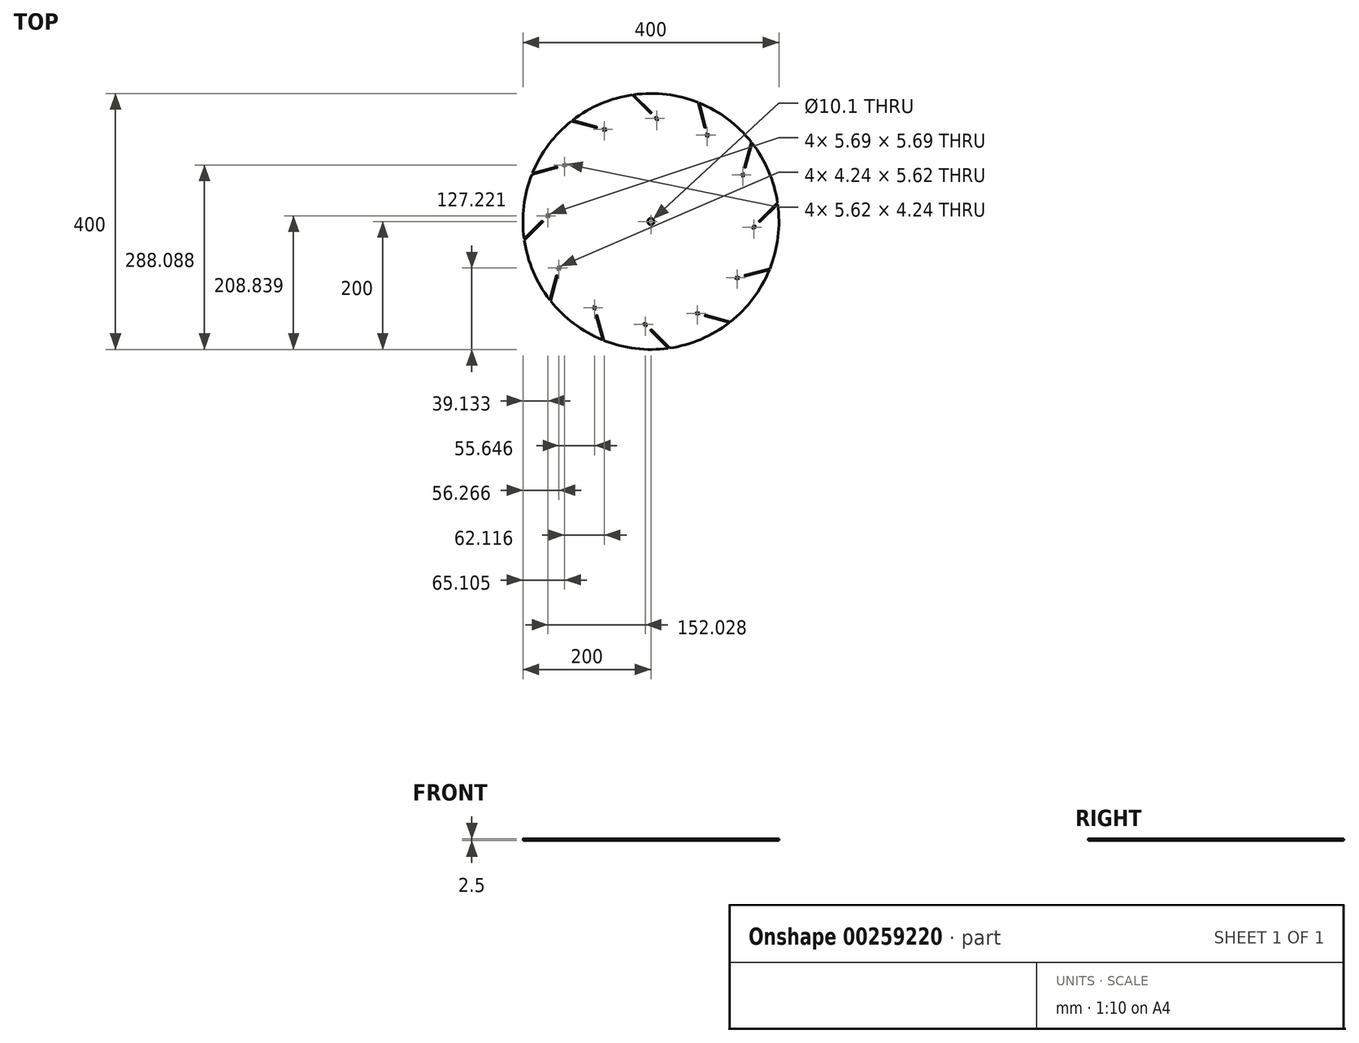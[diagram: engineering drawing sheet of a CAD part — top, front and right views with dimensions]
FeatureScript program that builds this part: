
annotation { "Feature Type Name" : "Feature", "Feature Type Description" : "" }
export const myFeature = defineFeature(function(context is Context, id is Id, definition is map)
    precondition{}
    {
        {
            var Q0;
            Q0=qCreatedBy(makeId("Top.planeOp"),FACE);
            var sketch = newSketch(context, id + "F0", { "sketchPlane" : qUnion([Q0])});
            skArc(sketch, "E0", {"start": v(-197.85, -29.24) * mm, "mid": v(-184.02, -78.33) * mm, "end": v(-158.23, -122.33) * mm});
            skLineSegment(sketch, "E1", {"start": v(28.28, 28.28) * mm, "end": v(-28.28, -28.28) * mm, "construction": true});
            skCircle(sketch, "E2", {"center": v(0, 0) * mm, "radius": 40 * mm, "construction": true});
            skLineSegment(sketch, "E3", {"start": v(40, 0) * mm, "end": v(-286.23, 0) * mm, "construction": true});
            skLineSegment(sketch, "E4", {"start": v(-28.28, -28.28) * mm, "end": v(-235.32, -28.28) * mm, "construction": true});
            skLineSegment(sketch, "E5", {"start": v(-197.99, -28.28) * mm, "end": v(-113.58, 56.13) * mm, "construction": true});
            skPoint(sketch, "E6", {"position": v(-169.7, 0) * mm});
            skCircle(sketch, "E7", {"center": v(0, 0) * mm, "radius": 169.7 * mm, "construction": true});
            skCircle(sketch, "E8", {"center": v(-169.7, 0) * mm, "radius": 0.78 * mm, "construction": true});
            skPoint(sketch, "E9", {"position": v(-197.99, -28.28) * mm});
            skLineSegment(sketch, "E10", {"start": v(-197.44, -28.83) * mm, "end": v(-198.54, -27.74) * mm, "construction": true});
            skCircle(sketch, "E11", {"center": v(-169.7, 0) * mm, "radius": 40 * mm, "construction": true});
            skLineSegment(sketch, "E12.trimOffspring", {"start": v(-170.36, 0.44) * mm, "end": v(-197.62, -26.82) * mm});
            skLineSegment(sketch, "E13.trimOffspring", {"start": v(-169.26, -0.65) * mm, "end": v(-197.85, -29.24) * mm});
            skLineSegment(sketch, "E14", {"start": v(-170.15, 0.44) * mm, "end": v(-169.26, -0.44) * mm});
            skLineSegment(sketch, "E15.MirrorCS", {"start": v(-170.25, 0.55) * mm, "end": v(-141.97, 28.83) * mm, "construction": true});
            skLineSegment(sketch, "E16.MirrorCS", {"start": v(-169.16, -0.55) * mm, "end": v(-140.87, 27.74) * mm, "construction": true});
            skLineSegment(sketch, "E17.MirrorCS", {"start": v(-140.87, 27.74) * mm, "end": v(-141.97, 28.83) * mm, "construction": true});
            skLineSegment(sketch, "E18", {"start": v(-163.71, 8.15) * mm, "end": v(-161.56, 6) * mm});
            skLineSegment(sketch, "E19", {"start": v(-160.18, 11.68) * mm, "end": v(-158.02, 9.53) * mm});
            skLineSegment(sketch, "E20.trimOffspring", {"start": v(-161.56, 6) * mm, "end": v(-158.02, 9.53) * mm});
            skLineSegment(sketch, "E21.trimOffspring", {"start": v(-163.71, 8.15) * mm, "end": v(-160.18, 11.68) * mm});
            skLineSegment(sketch, "E22.trimOffspring", {"start": v(-198.53, -27.73) * mm, "end": v(-198.54, -27.74) * mm});
            skCircle(sketch, "E23", {"center": v(0, 0) * mm, "radius": 5.05 * mm});
            skArc(sketch, "E24", {"start": v(-170.15, 0.44) * mm, "mid": v(-170.25, 0.7) * mm, "end": v(-170.36, 0.44) * mm});
            skArc(sketch, "E25.MirrorC", {"start": v(-169.26, -0.44) * mm, "mid": v(-169, -0.55) * mm, "end": v(-169.26, -0.65) * mm});
            skPoint(sketch, "E26.orphan", {"position": v(-198.12, -27.32) * mm});
            skLineSegment(sketch, "E27.trimOffspring", {"start": v(-197.62, -26.82) * mm, "end": v(-198.2, -26.82) * mm});
            skLineSegment(sketch, "E28.1.0", {"start": v(-184.56, 75.58) * mm, "end": v(-185.05, 75.87) * mm});
            skLineSegment(sketch, "E28.1.1", {"start": v(-147.31, 85.56) * mm, "end": v(-184.56, 75.58) * mm});
            skArc(sketch, "E28.1.2", {"start": v(-147.13, 85.46) * mm, "mid": v(-147.1, 85.73) * mm, "end": v(-147.31, 85.56) * mm});
            skLineSegment(sketch, "E28.1.3", {"start": v(-147.13, 85.46) * mm, "end": v(-146.8, 84.25) * mm});
            skArc(sketch, "E28.1.4", {"start": v(-146.8, 84.25) * mm, "mid": v(-146.64, 84.03) * mm, "end": v(-146.91, 84.07) * mm});
            skLineSegment(sketch, "E28.1.5", {"start": v(-146.91, 84.07) * mm, "end": v(-185.96, 73.6) * mm});
            skLineSegment(sketch, "E28.1.6", {"start": v(-137.7, 88.91) * mm, "end": v(-132.88, 90.2) * mm});
            skLineSegment(sketch, "E28.1.7", {"start": v(-132.88, 90.2) * mm, "end": v(-132.09, 87.26) * mm});
            skLineSegment(sketch, "E28.1.8", {"start": v(-136.92, 85.97) * mm, "end": v(-132.09, 87.26) * mm});
            skLineSegment(sketch, "E28.1.9", {"start": v(-137.7, 88.91) * mm, "end": v(-136.92, 85.97) * mm});
            skLineSegment(sketch, "E28.2.0", {"start": v(-122.04, 157.74) * mm, "end": v(-122.33, 158.23) * mm});
            skLineSegment(sketch, "E28.2.1", {"start": v(-84.8, 147.76) * mm, "end": v(-122.04, 157.74) * mm});
            skArc(sketch, "E28.2.2", {"start": v(-84.7, 147.57) * mm, "mid": v(-84.52, 147.8) * mm, "end": v(-84.8, 147.76) * mm});
            skLineSegment(sketch, "E28.2.3", {"start": v(-84.7, 147.57) * mm, "end": v(-85.01, 146.37) * mm});
            skArc(sketch, "E28.2.4", {"start": v(-85.01, 146.37) * mm, "mid": v(-84.98, 146.1) * mm, "end": v(-85.2, 146.26) * mm});
            skLineSegment(sketch, "E28.2.5", {"start": v(-85.2, 146.26) * mm, "end": v(-124.25, 156.72) * mm});
            skLineSegment(sketch, "E28.2.6", {"start": v(-74.8, 145.85) * mm, "end": v(-69.97, 144.56) * mm});
            skLineSegment(sketch, "E28.2.7", {"start": v(-69.97, 144.56) * mm, "end": v(-70.76, 141.61) * mm});
            skLineSegment(sketch, "E28.2.8", {"start": v(-75.59, 142.9) * mm, "end": v(-70.76, 141.61) * mm});
            skLineSegment(sketch, "E28.2.9", {"start": v(-74.8, 145.85) * mm, "end": v(-75.59, 142.9) * mm});
            skLineSegment(sketch, "E28.3.0", {"start": v(-26.82, 197.62) * mm, "end": v(-26.82, 198.2) * mm});
            skLineSegment(sketch, "E28.3.1", {"start": v(0.44, 170.36) * mm, "end": v(-26.82, 197.62) * mm});
            skArc(sketch, "E28.3.2", {"start": v(0.44, 170.15) * mm, "mid": v(0.7, 170.25) * mm, "end": v(0.44, 170.36) * mm});
            skLineSegment(sketch, "E28.3.3", {"start": v(0.44, 170.15) * mm, "end": v(-0.44, 169.26) * mm});
            skArc(sketch, "E28.3.4", {"start": v(-0.44, 169.26) * mm, "mid": v(-0.55, 169) * mm, "end": v(-0.65, 169.26) * mm});
            skLineSegment(sketch, "E28.3.5", {"start": v(-0.65, 169.26) * mm, "end": v(-29.24, 197.85) * mm});
            skLineSegment(sketch, "E28.3.6", {"start": v(8.15, 163.71) * mm, "end": v(11.68, 160.18) * mm});
            skLineSegment(sketch, "E28.3.7", {"start": v(11.68, 160.18) * mm, "end": v(9.53, 158.02) * mm});
            skLineSegment(sketch, "E28.3.8", {"start": v(6, 161.56) * mm, "end": v(9.53, 158.02) * mm});
            skLineSegment(sketch, "E28.3.9", {"start": v(8.15, 163.71) * mm, "end": v(6, 161.56) * mm});
            skLineSegment(sketch, "E28.4.0", {"start": v(75.58, 184.56) * mm, "end": v(75.87, 185.05) * mm});
            skLineSegment(sketch, "E28.4.1", {"start": v(85.56, 147.31) * mm, "end": v(75.58, 184.56) * mm});
            skArc(sketch, "E28.4.2", {"start": v(85.46, 147.13) * mm, "mid": v(85.73, 147.1) * mm, "end": v(85.56, 147.31) * mm});
            skLineSegment(sketch, "E28.4.3", {"start": v(85.46, 147.13) * mm, "end": v(84.25, 146.8) * mm});
            skArc(sketch, "E28.4.4", {"start": v(84.25, 146.8) * mm, "mid": v(84.03, 146.64) * mm, "end": v(84.07, 146.91) * mm});
            skLineSegment(sketch, "E28.4.5", {"start": v(84.07, 146.91) * mm, "end": v(73.6, 185.96) * mm});
            skLineSegment(sketch, "E28.4.6", {"start": v(88.91, 137.7) * mm, "end": v(90.2, 132.88) * mm});
            skLineSegment(sketch, "E28.4.7", {"start": v(90.2, 132.88) * mm, "end": v(87.26, 132.09) * mm});
            skLineSegment(sketch, "E28.4.8", {"start": v(85.97, 136.92) * mm, "end": v(87.26, 132.09) * mm});
            skLineSegment(sketch, "E28.4.9", {"start": v(88.91, 137.7) * mm, "end": v(85.97, 136.92) * mm});
            skLineSegment(sketch, "E28.5.0", {"start": v(157.74, 122.04) * mm, "end": v(158.23, 122.33) * mm});
            skLineSegment(sketch, "E28.5.1", {"start": v(147.76, 84.8) * mm, "end": v(157.74, 122.04) * mm});
            skArc(sketch, "E28.5.2", {"start": v(147.57, 84.7) * mm, "mid": v(147.8, 84.52) * mm, "end": v(147.76, 84.8) * mm});
            skLineSegment(sketch, "E28.5.3", {"start": v(147.57, 84.7) * mm, "end": v(146.37, 85.01) * mm});
            skArc(sketch, "E28.5.4", {"start": v(146.37, 85.01) * mm, "mid": v(146.1, 84.98) * mm, "end": v(146.26, 85.2) * mm});
            skLineSegment(sketch, "E28.5.5", {"start": v(146.26, 85.2) * mm, "end": v(156.72, 124.25) * mm});
            skLineSegment(sketch, "E28.5.6", {"start": v(145.85, 74.8) * mm, "end": v(144.56, 69.97) * mm});
            skLineSegment(sketch, "E28.5.7", {"start": v(144.56, 69.97) * mm, "end": v(141.61, 70.76) * mm});
            skLineSegment(sketch, "E28.5.8", {"start": v(142.9, 75.59) * mm, "end": v(141.61, 70.76) * mm});
            skLineSegment(sketch, "E28.5.9", {"start": v(145.85, 74.8) * mm, "end": v(142.9, 75.59) * mm});
            skLineSegment(sketch, "E28.6.0", {"start": v(197.62, 26.82) * mm, "end": v(198.2, 26.82) * mm});
            skLineSegment(sketch, "E28.6.1", {"start": v(170.36, -0.44) * mm, "end": v(197.62, 26.82) * mm});
            skArc(sketch, "E28.6.2", {"start": v(170.15, -0.44) * mm, "mid": v(170.25, -0.7) * mm, "end": v(170.36, -0.44) * mm});
            skLineSegment(sketch, "E28.6.3", {"start": v(170.15, -0.44) * mm, "end": v(169.26, 0.44) * mm});
            skArc(sketch, "E28.6.4", {"start": v(169.26, 0.44) * mm, "mid": v(169, 0.55) * mm, "end": v(169.26, 0.65) * mm});
            skLineSegment(sketch, "E28.6.5", {"start": v(169.26, 0.65) * mm, "end": v(197.85, 29.24) * mm});
            skLineSegment(sketch, "E28.6.6", {"start": v(163.71, -8.15) * mm, "end": v(160.18, -11.68) * mm});
            skLineSegment(sketch, "E28.6.7", {"start": v(160.18, -11.68) * mm, "end": v(158.02, -9.53) * mm});
            skLineSegment(sketch, "E28.6.8", {"start": v(161.56, -6) * mm, "end": v(158.02, -9.53) * mm});
            skLineSegment(sketch, "E28.6.9", {"start": v(163.71, -8.15) * mm, "end": v(161.56, -6) * mm});
            skLineSegment(sketch, "E28.7.0", {"start": v(184.56, -75.58) * mm, "end": v(185.05, -75.87) * mm});
            skLineSegment(sketch, "E28.7.1", {"start": v(147.31, -85.56) * mm, "end": v(184.56, -75.58) * mm});
            skArc(sketch, "E28.7.2", {"start": v(147.13, -85.46) * mm, "mid": v(147.1, -85.73) * mm, "end": v(147.31, -85.56) * mm});
            skLineSegment(sketch, "E28.7.3", {"start": v(147.13, -85.46) * mm, "end": v(146.8, -84.25) * mm});
            skArc(sketch, "E28.7.4", {"start": v(146.8, -84.25) * mm, "mid": v(146.64, -84.03) * mm, "end": v(146.91, -84.07) * mm});
            skLineSegment(sketch, "E28.7.5", {"start": v(146.91, -84.07) * mm, "end": v(185.96, -73.6) * mm});
            skLineSegment(sketch, "E28.7.6", {"start": v(137.7, -88.91) * mm, "end": v(132.88, -90.2) * mm});
            skLineSegment(sketch, "E28.7.7", {"start": v(132.88, -90.2) * mm, "end": v(132.09, -87.26) * mm});
            skLineSegment(sketch, "E28.7.8", {"start": v(136.92, -85.97) * mm, "end": v(132.09, -87.26) * mm});
            skLineSegment(sketch, "E28.7.9", {"start": v(137.7, -88.91) * mm, "end": v(136.92, -85.97) * mm});
            skLineSegment(sketch, "E28.8.0", {"start": v(122.04, -157.74) * mm, "end": v(122.33, -158.23) * mm});
            skLineSegment(sketch, "E28.8.1", {"start": v(84.8, -147.76) * mm, "end": v(122.04, -157.74) * mm});
            skArc(sketch, "E28.8.2", {"start": v(84.7, -147.57) * mm, "mid": v(84.52, -147.8) * mm, "end": v(84.8, -147.76) * mm});
            skLineSegment(sketch, "E28.8.3", {"start": v(84.7, -147.57) * mm, "end": v(85.01, -146.37) * mm});
            skArc(sketch, "E28.8.4", {"start": v(85.01, -146.37) * mm, "mid": v(84.98, -146.1) * mm, "end": v(85.2, -146.26) * mm});
            skLineSegment(sketch, "E28.8.5", {"start": v(85.2, -146.26) * mm, "end": v(124.25, -156.72) * mm});
            skLineSegment(sketch, "E28.8.6", {"start": v(74.8, -145.85) * mm, "end": v(69.97, -144.56) * mm});
            skLineSegment(sketch, "E28.8.7", {"start": v(69.97, -144.56) * mm, "end": v(70.76, -141.61) * mm});
            skLineSegment(sketch, "E28.8.8", {"start": v(75.59, -142.9) * mm, "end": v(70.76, -141.61) * mm});
            skLineSegment(sketch, "E28.8.9", {"start": v(74.8, -145.85) * mm, "end": v(75.59, -142.9) * mm});
            skLineSegment(sketch, "E28.9.0", {"start": v(26.82, -197.62) * mm, "end": v(26.82, -198.2) * mm});
            skLineSegment(sketch, "E28.9.1", {"start": v(-0.44, -170.36) * mm, "end": v(26.82, -197.62) * mm});
            skArc(sketch, "E28.9.2", {"start": v(-0.44, -170.15) * mm, "mid": v(-0.7, -170.25) * mm, "end": v(-0.44, -170.36) * mm});
            skLineSegment(sketch, "E28.9.3", {"start": v(-0.44, -170.15) * mm, "end": v(0.44, -169.26) * mm});
            skArc(sketch, "E28.9.4", {"start": v(0.44, -169.26) * mm, "mid": v(0.55, -169) * mm, "end": v(0.65, -169.26) * mm});
            skLineSegment(sketch, "E28.9.5", {"start": v(0.65, -169.26) * mm, "end": v(29.24, -197.85) * mm});
            skLineSegment(sketch, "E28.9.6", {"start": v(-8.15, -163.71) * mm, "end": v(-11.68, -160.18) * mm});
            skLineSegment(sketch, "E28.9.7", {"start": v(-11.68, -160.18) * mm, "end": v(-9.53, -158.02) * mm});
            skLineSegment(sketch, "E28.9.8", {"start": v(-6, -161.56) * mm, "end": v(-9.53, -158.02) * mm});
            skLineSegment(sketch, "E28.9.9", {"start": v(-8.15, -163.71) * mm, "end": v(-6, -161.56) * mm});
            skLineSegment(sketch, "E28.10.0", {"start": v(-75.58, -184.56) * mm, "end": v(-75.87, -185.05) * mm});
            skLineSegment(sketch, "E28.10.1", {"start": v(-85.56, -147.31) * mm, "end": v(-75.58, -184.56) * mm});
            skArc(sketch, "E28.10.2", {"start": v(-85.46, -147.13) * mm, "mid": v(-85.73, -147.1) * mm, "end": v(-85.56, -147.31) * mm});
            skLineSegment(sketch, "E28.10.3", {"start": v(-85.46, -147.13) * mm, "end": v(-84.25, -146.8) * mm});
            skArc(sketch, "E28.10.4", {"start": v(-84.25, -146.8) * mm, "mid": v(-84.03, -146.64) * mm, "end": v(-84.07, -146.91) * mm});
            skLineSegment(sketch, "E28.10.5", {"start": v(-84.07, -146.91) * mm, "end": v(-73.6, -185.96) * mm});
            skLineSegment(sketch, "E28.10.6", {"start": v(-88.91, -137.7) * mm, "end": v(-90.2, -132.88) * mm});
            skLineSegment(sketch, "E28.10.7", {"start": v(-90.2, -132.88) * mm, "end": v(-87.26, -132.09) * mm});
            skLineSegment(sketch, "E28.10.8", {"start": v(-85.97, -136.92) * mm, "end": v(-87.26, -132.09) * mm});
            skLineSegment(sketch, "E28.10.9", {"start": v(-88.91, -137.7) * mm, "end": v(-85.97, -136.92) * mm});
            skLineSegment(sketch, "E28.11.0", {"start": v(-157.74, -122.04) * mm, "end": v(-158.23, -122.33) * mm});
            skLineSegment(sketch, "E28.11.1", {"start": v(-147.76, -84.8) * mm, "end": v(-157.74, -122.04) * mm});
            skArc(sketch, "E28.11.2", {"start": v(-147.57, -84.7) * mm, "mid": v(-147.8, -84.52) * mm, "end": v(-147.76, -84.8) * mm});
            skLineSegment(sketch, "E28.11.3", {"start": v(-147.57, -84.7) * mm, "end": v(-146.37, -85.01) * mm});
            skArc(sketch, "E28.11.4", {"start": v(-146.37, -85.01) * mm, "mid": v(-146.1, -84.98) * mm, "end": v(-146.26, -85.2) * mm});
            skLineSegment(sketch, "E28.11.5", {"start": v(-146.26, -85.2) * mm, "end": v(-156.72, -124.25) * mm});
            skLineSegment(sketch, "E28.11.6", {"start": v(-145.85, -74.8) * mm, "end": v(-144.56, -69.97) * mm});
            skLineSegment(sketch, "E28.11.7", {"start": v(-144.56, -69.97) * mm, "end": v(-141.61, -70.76) * mm});
            skLineSegment(sketch, "E28.11.8", {"start": v(-142.9, -75.59) * mm, "end": v(-141.61, -70.76) * mm});
            skLineSegment(sketch, "E28.11.9", {"start": v(-145.85, -74.8) * mm, "end": v(-142.9, -75.59) * mm});
            skLineSegment(sketch, "E28.anchor1", {"start": v(0, 0) * mm, "end": v(-198.2, -26.82) * mm, "construction": true});
            skLineSegment(sketch, "E28.anchor2", {"start": v(0, 0) * mm, "end": v(-158.23, -122.33) * mm, "construction": true});
            skArc(sketch, "E29.trimOffspring", {"start": v(-185.96, 73.6) * mm, "mid": v(-198.53, 24.18) * mm, "end": v(-198.2, -26.82) * mm});
            skArc(sketch, "E30.trimOffspring", {"start": v(-124.25, 156.72) * mm, "mid": v(-159.85, 120.2) * mm, "end": v(-185.05, 75.87) * mm});
            skArc(sketch, "E31.trimOffspring", {"start": v(-29.24, 197.85) * mm, "mid": v(-78.33, 184.02) * mm, "end": v(-122.33, 158.23) * mm});
            skArc(sketch, "E32.trimOffspring", {"start": v(73.6, 185.96) * mm, "mid": v(24.18, 198.53) * mm, "end": v(-26.82, 198.2) * mm});
            skArc(sketch, "E33.trimOffspring", {"start": v(156.72, 124.25) * mm, "mid": v(120.2, 159.85) * mm, "end": v(75.87, 185.05) * mm});
            skArc(sketch, "E34.trimOffspring", {"start": v(197.85, 29.24) * mm, "mid": v(184.02, 78.33) * mm, "end": v(158.23, 122.33) * mm});
            skArc(sketch, "E35.trimOffspring", {"start": v(185.96, -73.6) * mm, "mid": v(198.53, -24.18) * mm, "end": v(198.2, 26.82) * mm});
            skArc(sketch, "E36.trimOffspring", {"start": v(124.25, -156.72) * mm, "mid": v(159.85, -120.2) * mm, "end": v(185.05, -75.87) * mm});
            skArc(sketch, "E37.trimOffspring", {"start": v(29.24, -197.85) * mm, "mid": v(78.33, -184.02) * mm, "end": v(122.33, -158.23) * mm});
            skArc(sketch, "E38.trimOffspring", {"start": v(-73.6, -185.96) * mm, "mid": v(-24.18, -198.53) * mm, "end": v(26.82, -198.2) * mm});
            skArc(sketch, "E39.trimOffspring", {"start": v(-156.72, -124.25) * mm, "mid": v(-120.2, -159.85) * mm, "end": v(-75.87, -185.05) * mm});
            skSolve(sketch);
        }
        {
            var Q0;
            Q0=qSketchRegion(id+"F0",true);
            extrude(context, id + "F1", {"entities" : qUnion([Q0]), "depth" : 1.25 * mm, "hasSecondDirection" : true, "secondDirectionOppositeDirection" : true, "secondDirectionDepth" : 1.25 * mm});
        }
    });
